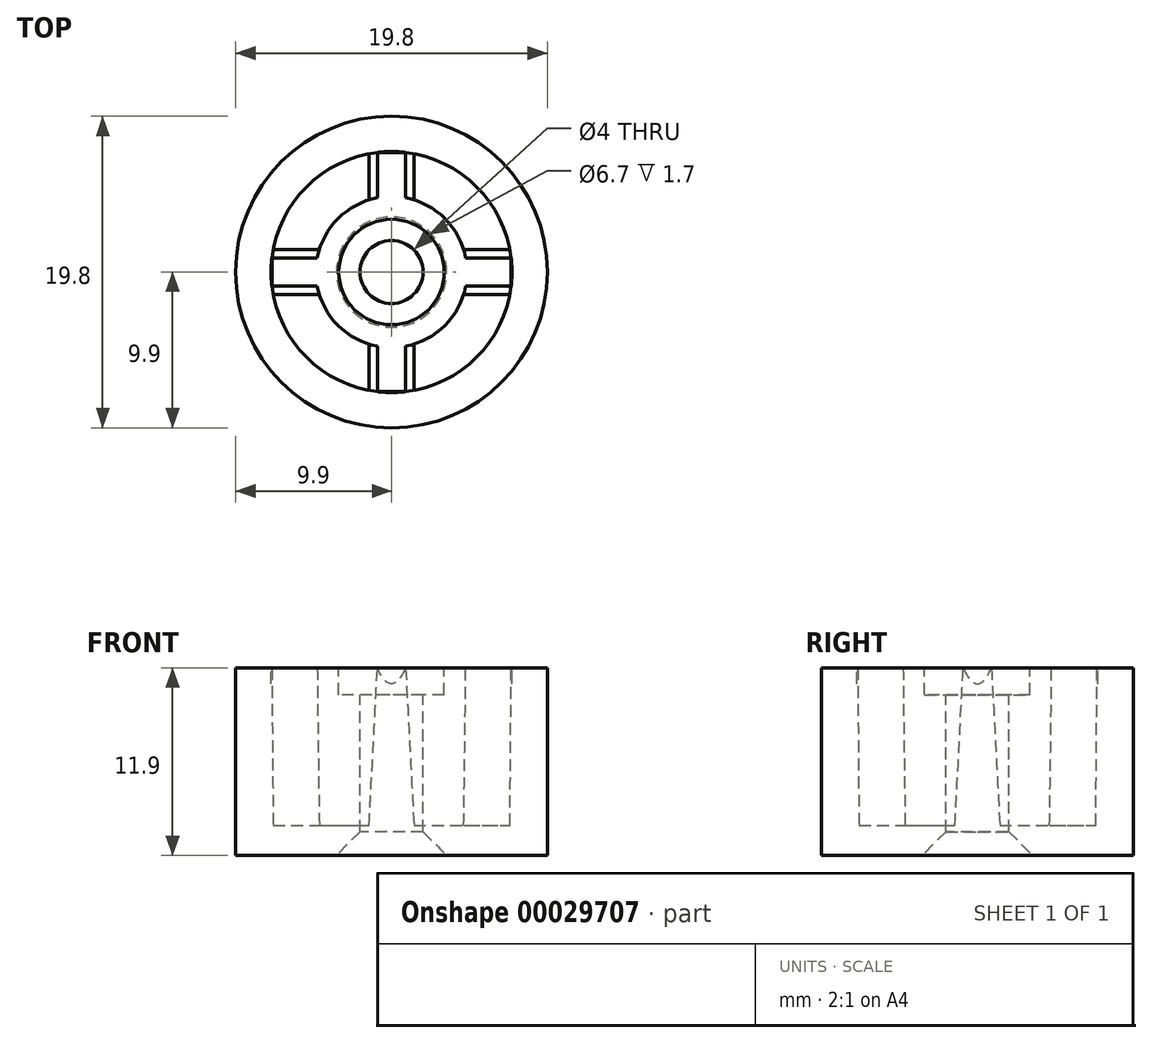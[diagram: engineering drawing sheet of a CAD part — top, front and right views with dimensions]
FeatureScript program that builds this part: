
annotation { "Feature Type Name" : "Feature", "Feature Type Description" : "" }
export const myFeature = defineFeature(function(context is Context, id is Id, definition is map)
    precondition{}
    {
        {
            var Q0;
            Q0=qCreatedBy(makeId("Top.planeOp"),FACE);
            var sketch = newSketch(context, id + "F0", { "sketchPlane" : qUnion([Q0])});
            skCircle(sketch, "E0", {"center": v(0, 0) * mm, "radius": 9.9 * mm});
            skSolve(sketch);
        }
        {
            var Q0;
            Q0 = qSketchRegion(id + "F0", true);
            extrude(context, id + "F1", {"entities" : qUnion([Q0]), "depth" : 11.9 * mm, "offsetDistance" : 25 * mm});
        }
        {
            var Q0;
            Q0=makeQuery(id+"F1.opExtrude","CAP_FACE",FACE,{"disambiguationData":[OSD([sQuery(id+"F0.wireOp",EDGE,"E0")])],"isStart":false});
            var sketch = newSketch(context, id + "F2", { "sketchPlane" : qUnion([Q0])});
            skCircle(sketch, "E1", {"center": v(0, 0) * mm, "radius": 7.65 * mm});
            skSolve(sketch);
        }
        {
            var Q0;
            Q0 = qSketchRegion(id + "F2", true);
            extrude(context, id + "F3", {"entities" : qUnion([Q0]), "operationType" : NewBodyOperationType.REMOVE, "oppositeDirection" : true, "depth" : 10 * mm, "offsetDistance" : 25 * mm});
        }
        {
            var Q0;
            Q0=makeQuery(id+"F3.boolean.opBoolean","COPY",FACE,{"derivedFrom":makeQuery(id+"F3.opExtrude","CAP_FACE",FACE,{"disambiguationData":[OSD([sQuery(id+"F2.wireOp",EDGE,"E1")])],"isStart":false})});
            var sketch = newSketch(context, id + "F4", { "sketchPlane" : qUnion([Q0])});
            skCircle(sketch, "E2", {"center": v(0, 0) * mm, "radius": 4.8 * mm});
            skSolve(sketch);
        }
        {
            var Q0;
            Q0 = qSketchRegion(id + "F4", true);
            extrude(context, id + "F5", {"entities" : qUnion([Q0]), "operationType" : NewBodyOperationType.ADD, "depth" : 10 * mm, "offsetDistance" : 25 * mm});
        }
        {
            var Q0;
            Q0=makeQuery(id+"F5.opExtrude","CAP_FACE",FACE,{"disambiguationData":[OSD([sQuery(id+"F4.wireOp",EDGE,"E2")])],"isStart":false});
            var sketch = newSketch(context, id + "F6", { "sketchPlane" : qUnion([Q0])});
            skLineSegment(sketch, "E3.bottom", {"start": v(0.9, 7.6) * mm, "end": v(-0.9, 7.6) * mm});
            skLineSegment(sketch, "E3.top", {"start": v(0.9, -7.6) * mm, "end": v(-0.9, -7.6) * mm});
            skLineSegment(sketch, "E3.left", {"start": v(0.9, 7.6) * mm, "end": v(0.9, -7.6) * mm});
            skLineSegment(sketch, "E3.right", {"start": v(-0.9, 7.6) * mm, "end": v(-0.9, -7.6) * mm});
            skPoint(sketch, "E3.middle", {"position": v(0, 0) * mm});
            skLineSegment(sketch, "E4.bottom", {"start": v(7.6, -0.9) * mm, "end": v(-7.6, -0.9) * mm});
            skLineSegment(sketch, "E4.top", {"start": v(7.6, 0.9) * mm, "end": v(-7.6, 0.9) * mm});
            skLineSegment(sketch, "E4.left", {"start": v(7.6, -0.9) * mm, "end": v(7.6, 0.9) * mm});
            skLineSegment(sketch, "E4.right", {"start": v(-7.6, -0.9) * mm, "end": v(-7.6, 0.9) * mm});
            skSolve(sketch);
        }
        {
            var Q0;
            Q0 = qSketchRegion(id + "F6", true);
            extrude(context, id + "F7", {"entities" : qUnion([Q0]), "operationType" : NewBodyOperationType.ADD, "oppositeDirection" : true, "depth" : 10 * mm, "offsetDistance" : 25 * mm, "hasDraft" : true, "draftAngle" : 3 * degree});
        }
        {
            var Q0;
            Q0=makeQuery(id+"F7.boolean.opBoolean","MERGE",FACE,{"derivedFrom":[makeQuery(id+"F5.opExtrude","CAP_FACE",FACE,{"disambiguationData":[OSD([sQuery(id+"F4.wireOp",EDGE,"E2")])],"isStart":false}),makeQuery(id+"F7.opExtrude","CAP_FACE",FACE,{"disambiguationData":[OSD([sQuery(id+"F6.wireOp",EDGE,"E3.bottom"),sQuery(id+"F6.wireOp",EDGE,"E3.top"),sQuery(id+"F6.wireOp",EDGE,"E3.left"),sQuery(id+"F6.wireOp",EDGE,"E3.right"),sQuery(id+"F6.wireOp",EDGE,"E4.bottom"),sQuery(id+"F6.wireOp",EDGE,"E4.top"),sQuery(id+"F6.wireOp",EDGE,"E4.left"),sQuery(id+"F6.wireOp",EDGE,"E4.right")])],"isStart":true})]});
            var sketch = newSketch(context, id + "F8", { "sketchPlane" : qUnion([Q0])});
            skCircle(sketch, "E5", {"center": v(0, 0) * mm, "radius": 2 * mm});
            skSolve(sketch);
        }
        {
            var Q0;
            Q0 = qSketchRegion(id + "F8", true);
            extrude(context, id + "F9", {"entities" : qUnion([Q0]), "operationType" : NewBodyOperationType.REMOVE, "oppositeDirection" : true, "depth" : 25 * mm, "offsetDistance" : 25 * mm});
        }
        {
            var Q0;
            Q0=makeQuery(id+"F7.boolean.opBoolean","MERGE",FACE,{"derivedFrom":[makeQuery(id+"F5.opExtrude","CAP_FACE",FACE,{"disambiguationData":[OSD([sQuery(id+"F4.wireOp",EDGE,"E2")])],"isStart":false}),makeQuery(id+"F7.opExtrude","CAP_FACE",FACE,{"disambiguationData":[OSD([sQuery(id+"F6.wireOp",EDGE,"E3.bottom"),sQuery(id+"F6.wireOp",EDGE,"E3.top"),sQuery(id+"F6.wireOp",EDGE,"E3.left"),sQuery(id+"F6.wireOp",EDGE,"E3.right"),sQuery(id+"F6.wireOp",EDGE,"E4.bottom"),sQuery(id+"F6.wireOp",EDGE,"E4.top"),sQuery(id+"F6.wireOp",EDGE,"E4.left"),sQuery(id+"F6.wireOp",EDGE,"E4.right")])],"isStart":true})]});
            var sketch = newSketch(context, id + "F10", { "sketchPlane" : qUnion([Q0])});
            skCircle(sketch, "E6", {"center": v(0, 0) * mm, "radius": 3.35 * mm});
            skSolve(sketch);
        }
        {
            var Q0;
            Q0 = qSketchRegion(id + "F10", true);
            extrude(context, id + "F11", {"entities" : qUnion([Q0]), "operationType" : NewBodyOperationType.REMOVE, "oppositeDirection" : true, "depth" : 1.7 * mm, "offsetDistance" : 25 * mm});
        }
        {
            var Q0;
            Q0=makeQuery(id+"F9.boolean.opBoolean","INTERSECT",EDGE,{"derivedFrom":[makeQuery(id+"F1.opExtrude","CAP_FACE",FACE,{"disambiguationData":[OSD([sQuery(id+"F0.wireOp",EDGE,"E0")])],"isStart":true}),makeQuery(id+"F9.opExtrude","SWEPT_FACE",FACE,{"disambiguationData":[OSD([sQuery(id+"F8.wireOp",EDGE,"E5")])]})]});
            chamfer(context, id + "F12", {"entities" : qUnion([Q0]), "width" : 1.5 * mm, "tangentPropagation" : true});
        }
    });
